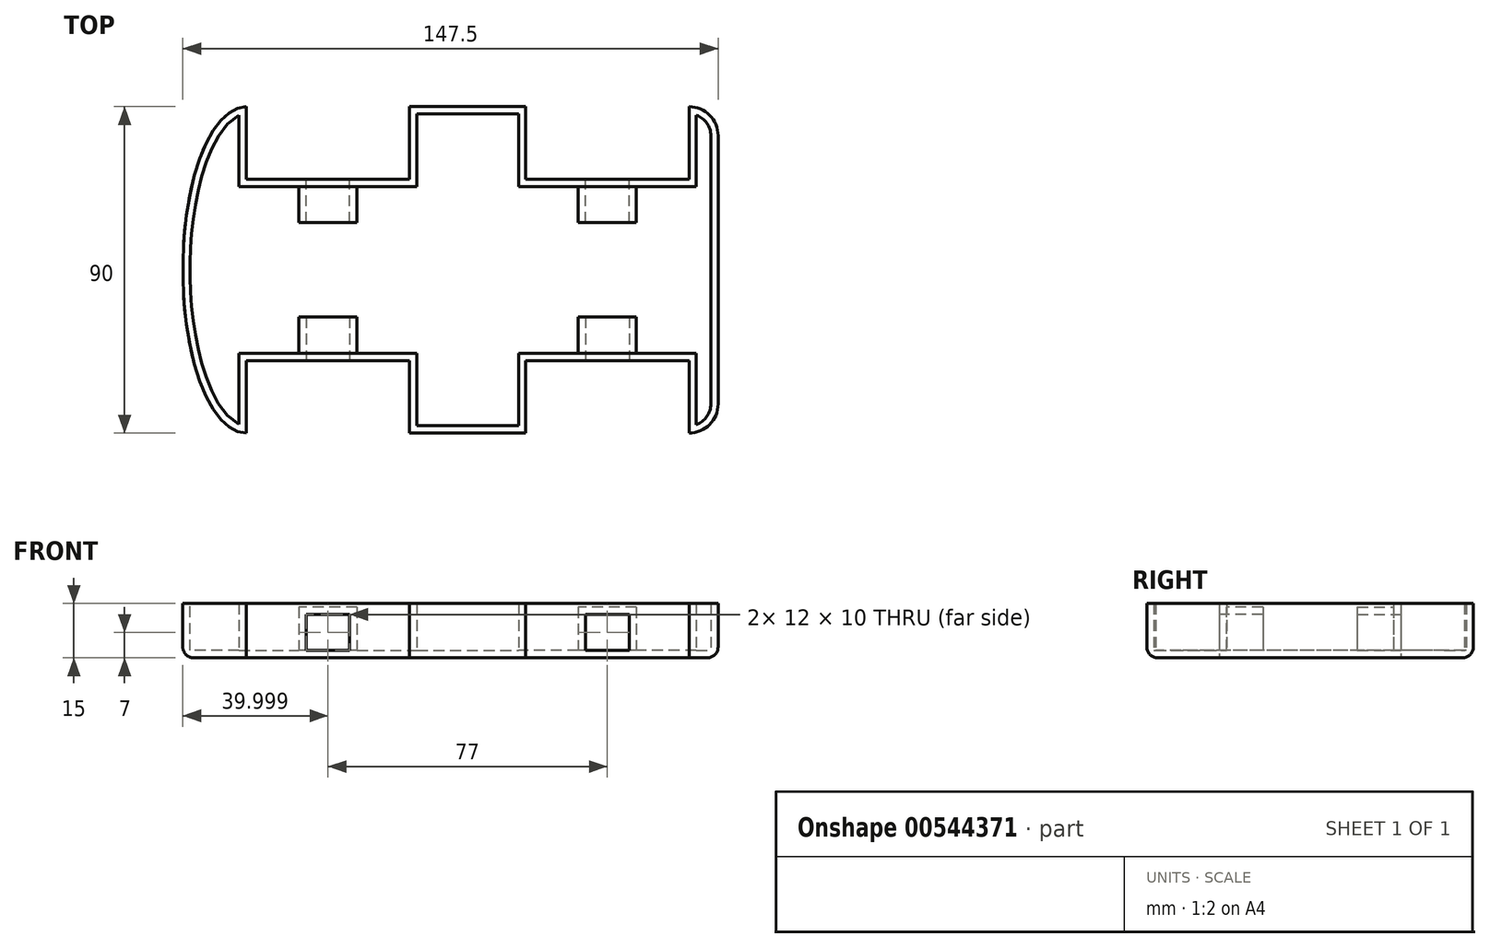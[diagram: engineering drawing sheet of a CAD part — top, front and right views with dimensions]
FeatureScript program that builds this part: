
annotation { "Feature Type Name" : "Feature", "Feature Type Description" : "" }
export const myFeature = defineFeature(function(context is Context, id is Id, definition is map)
    precondition{}
    {
        {
            var Q0;
            Q0=qCreatedBy(makeId("Top.planeOp"),FACE);
            var sketch = newSketch(context, id + "F0", { "sketchPlane" : qUnion([Q0])});
            skLineSegment(sketch, "E0.bottom", {"start": v(-27.96, 31.8) * mm, "end": v(4.04, 31.8) * mm});
            skLineSegment(sketch, "E0.top", {"start": v(-27.96, -58.2) * mm, "end": v(4.04, -58.2) * mm});
            skLineSegment(sketch, "E0.right", {"start": v(57.04, 23.8) * mm, "end": v(57.04, -50.2) * mm});
            skEllipticalArc(sketch, "E1", {});
            skPoint(sketch, "E2.visualSharp", {"position": v(57.04, 31.8) * mm});
            skArc(sketch, "E2.filletArc", {"start": v(57.04, 23.8) * mm, "mid": v(54.7, 29.46) * mm, "end": v(49.04, 31.8) * mm});
            skPoint(sketch, "E3.visualSharp", {"position": v(57.04, -58.2) * mm});
            skArc(sketch, "E3.filletArc", {"start": v(49.04, -58.2) * mm, "mid": v(54.7, -55.86) * mm, "end": v(57.04, -50.2) * mm});
            skLineSegment(sketch, "E4.top", {"start": v(-72.96, 11.8) * mm, "end": v(-27.96, 11.8) * mm});
            skLineSegment(sketch, "E4.left", {"start": v(-72.96, 31.8) * mm, "end": v(-72.96, 11.8) * mm});
            skLineSegment(sketch, "E4.right", {"start": v(-27.96, 31.8) * mm, "end": v(-27.96, 11.8) * mm});
            skLineSegment(sketch, "E5.top", {"start": v(49.04, 11.8) * mm, "end": v(4.04, 11.8) * mm});
            skLineSegment(sketch, "E5.left", {"start": v(49.04, 31.8) * mm, "end": v(49.04, 11.8) * mm});
            skLineSegment(sketch, "E5.right", {"start": v(4.04, 31.8) * mm, "end": v(4.04, 11.8) * mm});
            skLineSegment(sketch, "E6.top", {"start": v(-72.96, -38.2) * mm, "end": v(-27.96, -38.2) * mm});
            skLineSegment(sketch, "E6.left", {"start": v(-72.96, -58.2) * mm, "end": v(-72.96, -38.2) * mm});
            skLineSegment(sketch, "E6.right", {"start": v(-27.96, -58.2) * mm, "end": v(-27.96, -38.2) * mm});
            skLineSegment(sketch, "E7.top", {"start": v(49.04, -38.2) * mm, "end": v(4.04, -38.2) * mm});
            skLineSegment(sketch, "E7.left", {"start": v(49.04, -58.2) * mm, "end": v(49.04, -38.2) * mm});
            skLineSegment(sketch, "E7.right", {"start": v(4.04, -58.2) * mm, "end": v(4.04, -38.2) * mm});
            const initialGuessF0  = {"E1": [-0.07296122312545783, -0.013199719845870844, 0, 1, 0.045, 0.017502275273123383, 0, 3.141592653589793]};
            skSetInitialGuess(sketch, initialGuessF0);
            skSolve(sketch);
        }
        {
            var Q0;
            Q0=makeQuery(id+"F0.imprint","IMPRINT",FACE,{"disambiguationData":[TD([[makeQuery(id+"F0.imprint","IMPRINT",EDGE,{"derivedFrom":sQuery(id+"F0.wireOp",EDGE,"E0.bottom")}),-1.0]])]});
            extrude(context, id + "F1", {"entities" : qUnion([Q0]), "depth" : 15 * mm, "offsetDistance" : 25 * mm});
        }
        {
            var Q0;
            Q0=makeQuery(id+"F1.opExtrude","CAP_FACE",FACE,{"disambiguationData":[OSD([sQuery(id+"F0.wireOp",EDGE,"E0.bottom"),sQuery(id+"F0.wireOp",EDGE,"E0.top"),sQuery(id+"F0.wireOp",EDGE,"E0.right"),sQuery(id+"F0.wireOp",EDGE,"E1"),sQuery(id+"F0.wireOp",EDGE,"E2.filletArc"),sQuery(id+"F0.wireOp",EDGE,"E3.filletArc"),sQuery(id+"F0.wireOp",EDGE,"E4.top"),sQuery(id+"F0.wireOp",EDGE,"E4.left"),sQuery(id+"F0.wireOp",EDGE,"E4.right"),sQuery(id+"F0.wireOp",EDGE,"E5.top"),sQuery(id+"F0.wireOp",EDGE,"E5.left"),sQuery(id+"F0.wireOp",EDGE,"E5.right"),sQuery(id+"F0.wireOp",EDGE,"E6.top"),sQuery(id+"F0.wireOp",EDGE,"E6.left"),sQuery(id+"F0.wireOp",EDGE,"E6.right"),sQuery(id+"F0.wireOp",EDGE,"E7.top"),sQuery(id+"F0.wireOp",EDGE,"E7.left"),sQuery(id+"F0.wireOp",EDGE,"E7.right")])],"isStart":false});
            shell(context, id + "F2", {"entities" : qUnion([Q0]), "thickness" : 2 * mm});
        }
        {
            var Q0;
            Q0=makeQuery(id+"F1.opExtrude","CAP_EDGE",EDGE,{"disambiguationData":[OSD([sQuery(id+"F0.wireOp",EDGE,"E1")])],"isStart":true});
            var Q1;
            Q1=makeQuery(id+"F1.opExtrude","CAP_EDGE",EDGE,{"disambiguationData":[OSD([sQuery(id+"F0.wireOp",EDGE,"E0.top")])],"isStart":true});
            var Q2;
            Q2=makeQuery(id+"F1.opExtrude","CAP_EDGE",EDGE,{"disambiguationData":[OSD([sQuery(id+"F0.wireOp",EDGE,"E0.bottom")])],"isStart":true});
            var Q3;
            Q3=makeQuery(id+"F1.opExtrude","CAP_EDGE",EDGE,{"disambiguationData":[OSD([sQuery(id+"F0.wireOp",EDGE,"E0.right")])],"isStart":true});
            fillet(context, id + "F3", {"entities" : qUnion([Q0, Q1, Q2, Q3]), "radius" : 3 * mm, "tangentPropagation" : true, "allowEdgeOverflow" : false});
        }
        {
            var Q0;
            Q0=makeQuery(id+"F1.opExtrude","SWEPT_FACE",FACE,{"disambiguationData":[OSD([sQuery(id+"F0.wireOp",EDGE,"E6.top")])]});
            var sketch = newSketch(context, id + "F4", { "sketchPlane" : qUnion([Q0])});
            skLineSegment(sketch, "E8.bottom", {"start": v(-56.46, 12) * mm, "end": v(-44.46, 12) * mm});
            skLineSegment(sketch, "E8.top", {"start": v(-56.46, 2) * mm, "end": v(-44.46, 2) * mm});
            skLineSegment(sketch, "E8.left", {"start": v(-56.46, 12) * mm, "end": v(-56.46, 2) * mm});
            skLineSegment(sketch, "E8.right", {"start": v(-44.46, 12) * mm, "end": v(-44.46, 2) * mm});
            skSolve(sketch);
        }
        {
            var Q0;
            Q0=makeQuery(id+"F4.imprint","IMPRINT",FACE,{"disambiguationData":[TD([[makeQuery(id+"F4.imprint","IMPRINT",EDGE,{"derivedFrom":sQuery(id+"F4.wireOp",EDGE,"E8.bottom")}),1.0]])]});
            var sketch = newSketch(context, id + "F5", { "sketchPlane" : qUnion([Q0])});
            skLineSegment(sketch, "E9.bottom", {"start": v(-58.46, 14) * mm, "end": v(-42.46, 14) * mm});
            skLineSegment(sketch, "E9.top", {"start": v(-58.46, 2) * mm, "end": v(-42.46, 2) * mm});
            skLineSegment(sketch, "E9.left", {"start": v(-58.46, 14) * mm, "end": v(-58.46, 2) * mm});
            skLineSegment(sketch, "E9.right", {"start": v(-42.46, 14) * mm, "end": v(-42.46, 2) * mm});
            skSolve(sketch);
        }
        {
            var Q0;
            Q0 = qSketchRegion(id + "F5", true);
            extrude(context, id + "F6", {"entities" : qUnion([Q0]), "operationType" : NewBodyOperationType.ADD, "oppositeDirection" : true, "depth" : 12 * mm, "offsetDistance" : 25 * mm});
        }
        {
            var Q0;
            Q0 = qSketchRegion(id + "F4", true);
            extrude(context, id + "F7", {"entities" : qUnion([Q0]), "operationType" : NewBodyOperationType.REMOVE, "oppositeDirection" : true, "depth" : 12 * mm, "offsetDistance" : 25 * mm});
        }
        {
            var Q0;
            Q0=makeQuery(id+"F1.opExtrude","SWEPT_FACE",FACE,{"disambiguationData":[OSD([sQuery(id+"F0.wireOp",EDGE,"E4.top")])]});
            var sketch = newSketch(context, id + "F8", { "sketchPlane" : qUnion([Q0])});
            skLineSegment(sketch, "E10.bottom", {"start": v(42.46, 14) * mm, "end": v(58.46, 14) * mm});
            skLineSegment(sketch, "E10.top", {"start": v(42.46, 2) * mm, "end": v(58.46, 2) * mm});
            skLineSegment(sketch, "E10.left", {"start": v(42.46, 14) * mm, "end": v(42.46, 2) * mm});
            skLineSegment(sketch, "E10.right", {"start": v(58.46, 14) * mm, "end": v(58.46, 2) * mm});
            skSolve(sketch);
        }
        {
            var Q0;
            Q0=makeQuery(id+"F8.imprint","IMPRINT",FACE,{"disambiguationData":[TD([[makeQuery(id+"F8.imprint","IMPRINT",EDGE,{"derivedFrom":sQuery(id+"F8.wireOp",EDGE,"E10.bottom")}),1.0]])]});
            var sketch = newSketch(context, id + "F9", { "sketchPlane" : qUnion([Q0])});
            skLineSegment(sketch, "E11.bottom", {"start": v(44.46, 12) * mm, "end": v(56.46, 12) * mm});
            skLineSegment(sketch, "E11.top", {"start": v(44.46, 2) * mm, "end": v(56.46, 2) * mm});
            skLineSegment(sketch, "E11.left", {"start": v(44.46, 12) * mm, "end": v(44.46, 2) * mm});
            skLineSegment(sketch, "E11.right", {"start": v(56.46, 12) * mm, "end": v(56.46, 2) * mm});
            skSolve(sketch);
        }
        {
            var Q0;
            Q0 = qSketchRegion(id + "F8", true);
            extrude(context, id + "F10", {"entities" : qUnion([Q0]), "operationType" : NewBodyOperationType.ADD, "oppositeDirection" : true, "depth" : 12 * mm, "offsetDistance" : 25 * mm});
        }
        {
            var Q0;
            Q0 = qSketchRegion(id + "F9", true);
            extrude(context, id + "F11", {"entities" : qUnion([Q0]), "operationType" : NewBodyOperationType.REMOVE, "oppositeDirection" : true, "depth" : 12 * mm, "offsetDistance" : 25 * mm});
        }
        {
            var Q0;
            Q0=makeQuery(id+"F1.opExtrude","SWEPT_FACE",FACE,{"disambiguationData":[OSD([sQuery(id+"F0.wireOp",EDGE,"E7.top")])]});
            var sketch = newSketch(context, id + "F12", { "sketchPlane" : qUnion([Q0])});
            skLineSegment(sketch, "E12.bottom", {"start": v(18.54, 14) * mm, "end": v(34.54, 14) * mm});
            skLineSegment(sketch, "E12.top", {"start": v(18.54, 2) * mm, "end": v(34.54, 2) * mm});
            skLineSegment(sketch, "E12.left", {"start": v(18.54, 14) * mm, "end": v(18.54, 2) * mm});
            skLineSegment(sketch, "E12.right", {"start": v(34.54, 14) * mm, "end": v(34.54, 2) * mm});
            skSolve(sketch);
        }
        {
            var Q0;
            Q0=makeQuery(id+"F12.imprint","IMPRINT",FACE,{"disambiguationData":[TD([[makeQuery(id+"F12.imprint","IMPRINT",EDGE,{"derivedFrom":sQuery(id+"F12.wireOp",EDGE,"E12.bottom")}),1.0]])]});
            var sketch = newSketch(context, id + "F13", { "sketchPlane" : qUnion([Q0])});
            skLineSegment(sketch, "E13.bottom", {"start": v(20.54, 12) * mm, "end": v(32.54, 12) * mm});
            skLineSegment(sketch, "E13.top", {"start": v(20.54, 2) * mm, "end": v(32.54, 2) * mm});
            skLineSegment(sketch, "E13.left", {"start": v(20.54, 12) * mm, "end": v(20.54, 2) * mm});
            skLineSegment(sketch, "E13.right", {"start": v(32.54, 12) * mm, "end": v(32.54, 2) * mm});
            skSolve(sketch);
        }
        {
            var Q0;
            Q0 = qSketchRegion(id + "F12", true);
            extrude(context, id + "F14", {"entities" : qUnion([Q0]), "operationType" : NewBodyOperationType.ADD, "oppositeDirection" : true, "depth" : 12 * mm, "offsetDistance" : 25 * mm});
        }
        {
            var Q0;
            Q0 = qSketchRegion(id + "F13", true);
            extrude(context, id + "F15", {"entities" : qUnion([Q0]), "operationType" : NewBodyOperationType.REMOVE, "oppositeDirection" : true, "depth" : 12 * mm, "offsetDistance" : 25 * mm});
        }
        {
            var Q0;
            Q0=makeQuery(id+"F1.opExtrude","SWEPT_FACE",FACE,{"disambiguationData":[OSD([sQuery(id+"F0.wireOp",EDGE,"E5.top")])]});
            var sketch = newSketch(context, id + "F16", { "sketchPlane" : qUnion([Q0])});
            skLineSegment(sketch, "E14.bottom", {"start": v(-34.54, 14) * mm, "end": v(-18.54, 14) * mm});
            skLineSegment(sketch, "E14.top", {"start": v(-34.54, 2) * mm, "end": v(-18.54, 2) * mm});
            skLineSegment(sketch, "E14.left", {"start": v(-34.54, 14) * mm, "end": v(-34.54, 2) * mm});
            skLineSegment(sketch, "E14.right", {"start": v(-18.54, 14) * mm, "end": v(-18.54, 2) * mm});
            skSolve(sketch);
        }
        {
            var Q0;
            Q0=makeQuery(id+"F16.imprint","IMPRINT",FACE,{"disambiguationData":[TD([[makeQuery(id+"F16.imprint","IMPRINT",EDGE,{"derivedFrom":sQuery(id+"F16.wireOp",EDGE,"E14.bottom")}),1.0]])]});
            var sketch = newSketch(context, id + "F17", { "sketchPlane" : qUnion([Q0])});
            skLineSegment(sketch, "E15.bottom", {"start": v(-32.54, 12) * mm, "end": v(-20.54, 12) * mm});
            skLineSegment(sketch, "E15.top", {"start": v(-32.54, 2) * mm, "end": v(-20.54, 2) * mm});
            skLineSegment(sketch, "E15.left", {"start": v(-32.54, 12) * mm, "end": v(-32.54, 2) * mm});
            skLineSegment(sketch, "E15.right", {"start": v(-20.54, 12) * mm, "end": v(-20.54, 2) * mm});
            skSolve(sketch);
        }
        {
            var Q0;
            Q0 = qSketchRegion(id + "F16", true);
            extrude(context, id + "F18", {"entities" : qUnion([Q0]), "operationType" : NewBodyOperationType.ADD, "oppositeDirection" : true, "depth" : 12 * mm, "offsetDistance" : 25 * mm});
        }
        {
            var Q0;
            Q0=makeQuery(id+"F17.imprint","IMPRINT",FACE,{"disambiguationData":[TD([[makeQuery(id+"F17.imprint","IMPRINT",EDGE,{"derivedFrom":sQuery(id+"F17.wireOp",EDGE,"E15.bottom")}),-1.0]])]});
            extrude(context, id + "F19", {"entities" : qUnion([Q0]), "operationType" : NewBodyOperationType.REMOVE, "oppositeDirection" : true, "depth" : 12 * mm, "offsetDistance" : 25 * mm});
        }
    });
